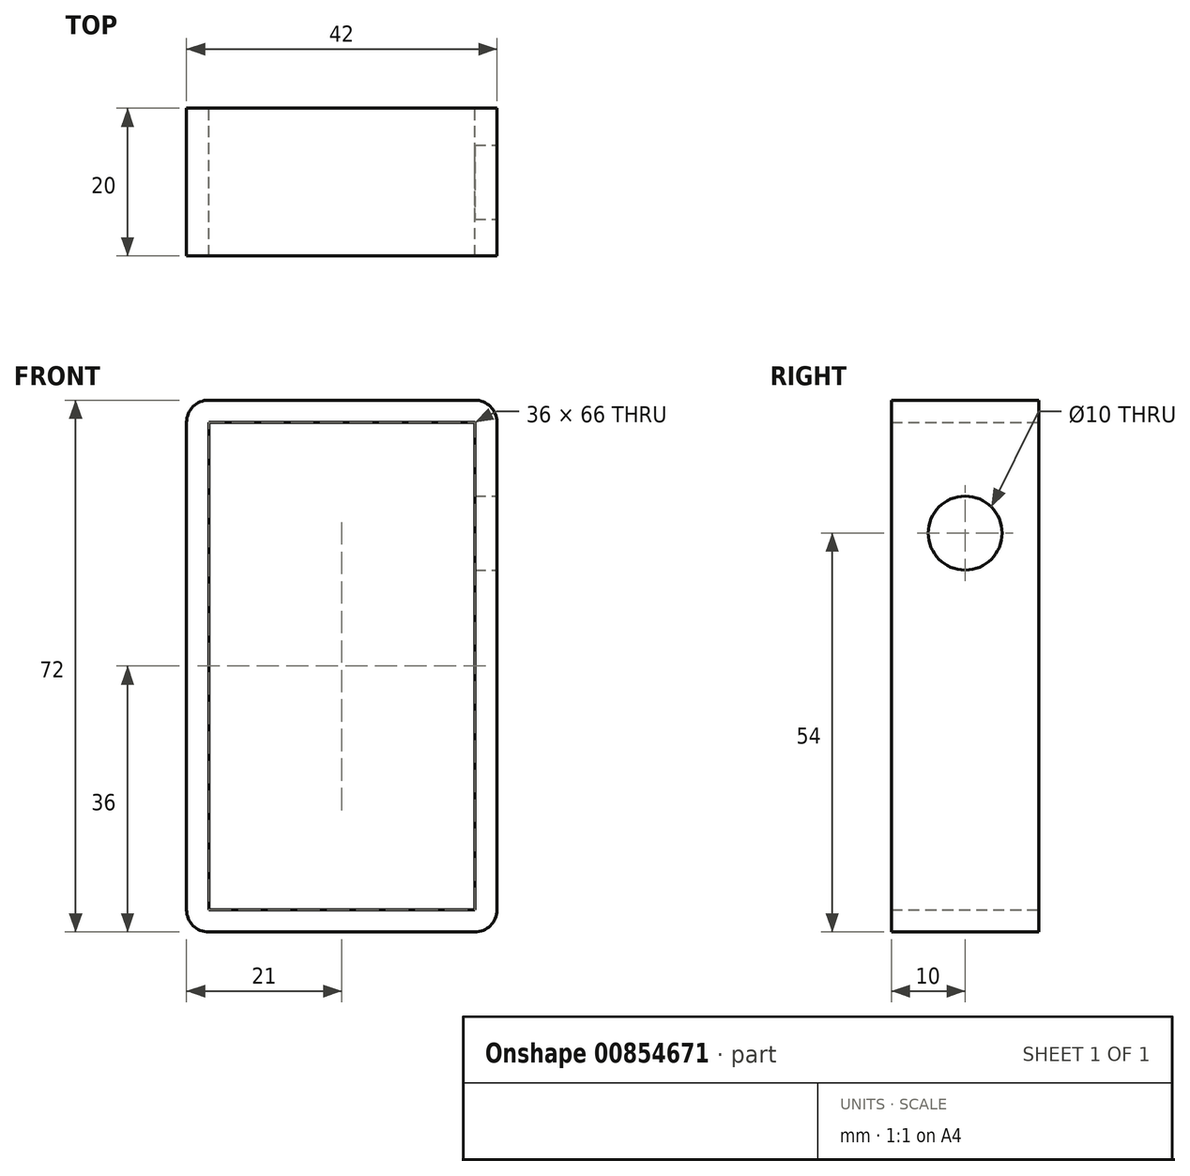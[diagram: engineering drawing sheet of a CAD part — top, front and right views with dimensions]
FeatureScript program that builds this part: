
annotation { "Feature Type Name" : "Feature", "Feature Type Description" : "" }
export const myFeature = defineFeature(function(context is Context, id is Id, definition is map)
    precondition{}
    {
        {
            var Q0;
            Q0=qCreatedBy(makeId("Front.planeOp"),FACE);
            var sketch = newSketch(context, id + "F0", { "sketchPlane" : qUnion([Q0])});
            skLineSegment(sketch, "E0.bottom", {"start": v(21, -36) * mm, "end": v(-21, -36) * mm});
            skLineSegment(sketch, "E0.top", {"start": v(21, 36) * mm, "end": v(-21, 36) * mm});
            skLineSegment(sketch, "E0.left", {"start": v(21, -36) * mm, "end": v(21, 36) * mm});
            skLineSegment(sketch, "E0.right", {"start": v(-21, -36) * mm, "end": v(-21, 36) * mm});
            skPoint(sketch, "E0.middle", {"position": v(0, 0) * mm});
            skLineSegment(sketch, "E1.bottom", {"start": v(18, -33) * mm, "end": v(-18, -33) * mm});
            skLineSegment(sketch, "E1.top", {"start": v(18, 33) * mm, "end": v(-18, 33) * mm});
            skLineSegment(sketch, "E1.left", {"start": v(18, -33) * mm, "end": v(18, 33) * mm});
            skLineSegment(sketch, "E1.right", {"start": v(-18, -33) * mm, "end": v(-18, 33) * mm});
            skSolve(sketch);
        }
        {
            var Q0;
            Q0 = qSketchRegion(id + "F0", true);
            extrude(context, id + "F1", {"entities" : qUnion([Q0]), "endBound" : BoundingType.SYMMETRIC, "depth" : 20 * mm, "offsetDistance" : 25 * mm});
        }
        {
            var Q0;
            Q0=makeQuery(id+"F1.opExtrude","SWEPT_EDGE",EDGE,{"disambiguationData":[OSD([sQuery(id+"F0.wireOp",EDGE,"E0.top"),sQuery(id+"F0.wireOp",EDGE,"E0.left")])]});
            var Q1;
            Q1=makeQuery(id+"F1.opExtrude","SWEPT_EDGE",EDGE,{"disambiguationData":[OSD([sQuery(id+"F0.wireOp",EDGE,"E0.top"),sQuery(id+"F0.wireOp",EDGE,"E0.right")])]});
            fillet(context, id + "F2", {"entities" : qUnion([Q0, Q1]), "radius" : 3 * mm, "tangentPropagation" : true, "allowEdgeOverflow" : false});
        }
        {
            var Q0;
            Q0=makeQuery(id+"F1.opExtrude","SWEPT_EDGE",EDGE,{"disambiguationData":[OSD([sQuery(id+"F0.wireOp",EDGE,"E0.bottom"),sQuery(id+"F0.wireOp",EDGE,"E0.left")])]});
            var Q1;
            Q1=makeQuery(id+"F1.opExtrude","SWEPT_EDGE",EDGE,{"disambiguationData":[OSD([sQuery(id+"F0.wireOp",EDGE,"E0.bottom"),sQuery(id+"F0.wireOp",EDGE,"E0.right")])]});
            fillet(context, id + "F3", {"entities" : qUnion([Q0, Q1]), "radius" : 3 * mm, "tangentPropagation" : true, "allowEdgeOverflow" : false});
        }
        {
            var Q0;
            Q0=makeQuery(id+"F1.opExtrude","SWEPT_FACE",FACE,{"disambiguationData":[OSD([sQuery(id+"F0.wireOp",EDGE,"E0.left")])]});
            var sketch = newSketch(context, id + "F4", { "sketchPlane" : qUnion([Q0])});
            skLineSegment(sketch, "E2", {"start": v(0, 33) * mm, "end": v(0, 18) * mm});
            skSolve(sketch);
        }
        {
            var Q0;
            Q0=sQuery(id+"F4.wireOp",VERTEX,"E2.end");
            var Q1;
            Q1=makeQuery(id+"F1.opExtrude","SWEPT_BODY",BODY,{"disambiguationData":[OSD([sQuery(id+"F0.wireOp",EDGE,"E0.bottom"),sQuery(id+"F0.wireOp",EDGE,"E0.top"),sQuery(id+"F0.wireOp",EDGE,"E0.left"),sQuery(id+"F0.wireOp",EDGE,"E0.right"),sQuery(id+"F0.wireOp",EDGE,"E1.bottom"),sQuery(id+"F0.wireOp",EDGE,"E1.top"),sQuery(id+"F0.wireOp",EDGE,"E1.left"),sQuery(id+"F0.wireOp",EDGE,"E1.right")])]});
            hole(context, id + "F5", {"style" : HoleStyle.SIMPLE, "endStyle" : HoleEndStyle.BLIND, "holeDiameter" : 10 * mm, "majorDiameter" : 5 * mm, "holeDepth" : 3 * mm, "isTappedThrough" : true, "tappedDepth" : 12 * mm, "tapClearance" : 3, "locations" : qUnion([Q0]), "scope" : qUnion([Q1])});
        }
    });
